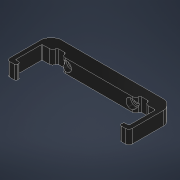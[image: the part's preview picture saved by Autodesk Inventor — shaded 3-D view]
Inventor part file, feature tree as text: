
AUTODESK INVENTOR PART (.ipt)
format: ipt  version: 2021 (Build 250183000, 183)  size: 233,984 bytes
history: native  units: mm
features: fillet x6, other x6, extrude x4, reference x2, plane x1, chamfer x1, hole x1, projected_geometry x1
ambient origin geometry x8: Origin, YZ Plane, XZ Plane, XY Plane, X Axis, Y Axis, Z Axis, Center Point
bodies: Solid1 (feature_tree)
feature tree (22):
  plane  "Work Plane1"
  extrude  "base"  Depth=67.0mm
  extrude  "holes_bolt_head"  Depth=38.0mm
  fillet  "bolt_head_fillet"  Radius=19.0mm
  extrude  "walls"  Depth=4.0mm
  fillet  "wall_top"  Radius=4.0mm
  fillet  "wall_tooth"  Radius=8.0mm
  chamfer  "wall_bottom"  Distance=5.8mm
  fillet  "wall_bottom_fillet"  Radius=5.8mm
  fillet  "inside"  Radius=3.2mm
  extrude  "groove_enclosure_bolt"  Depth=0.5mm
  fillet  "groove_enclosure_bolt_rounded"  Radius=15.7mm
  other  "base_sketch"
  reference  "Reference1"
  reference  "Reference2"
  hole  "holes_bolt_head_sketch"  [1 undecoded]
  other  "walls_sketch"
  projected_geometry  "Projected Loop1"
  other  "groove_enclosure_bolt_sketch"
  parser-record x1  (decoder bookkeeping rows leaked as tree rows — omitted from the tree; the rows remain in map.json)
  other  "plate_electronics.iam"
  other  "plate:1"
note: 1 required parameter value undecoded (feature->parameter linkage not recoverable at this tier; creation-order binding heuristic only, values carry confidence <= 0.55)
note: 1 file-system path scrubbed to <path> (originals preserved in map.json)
